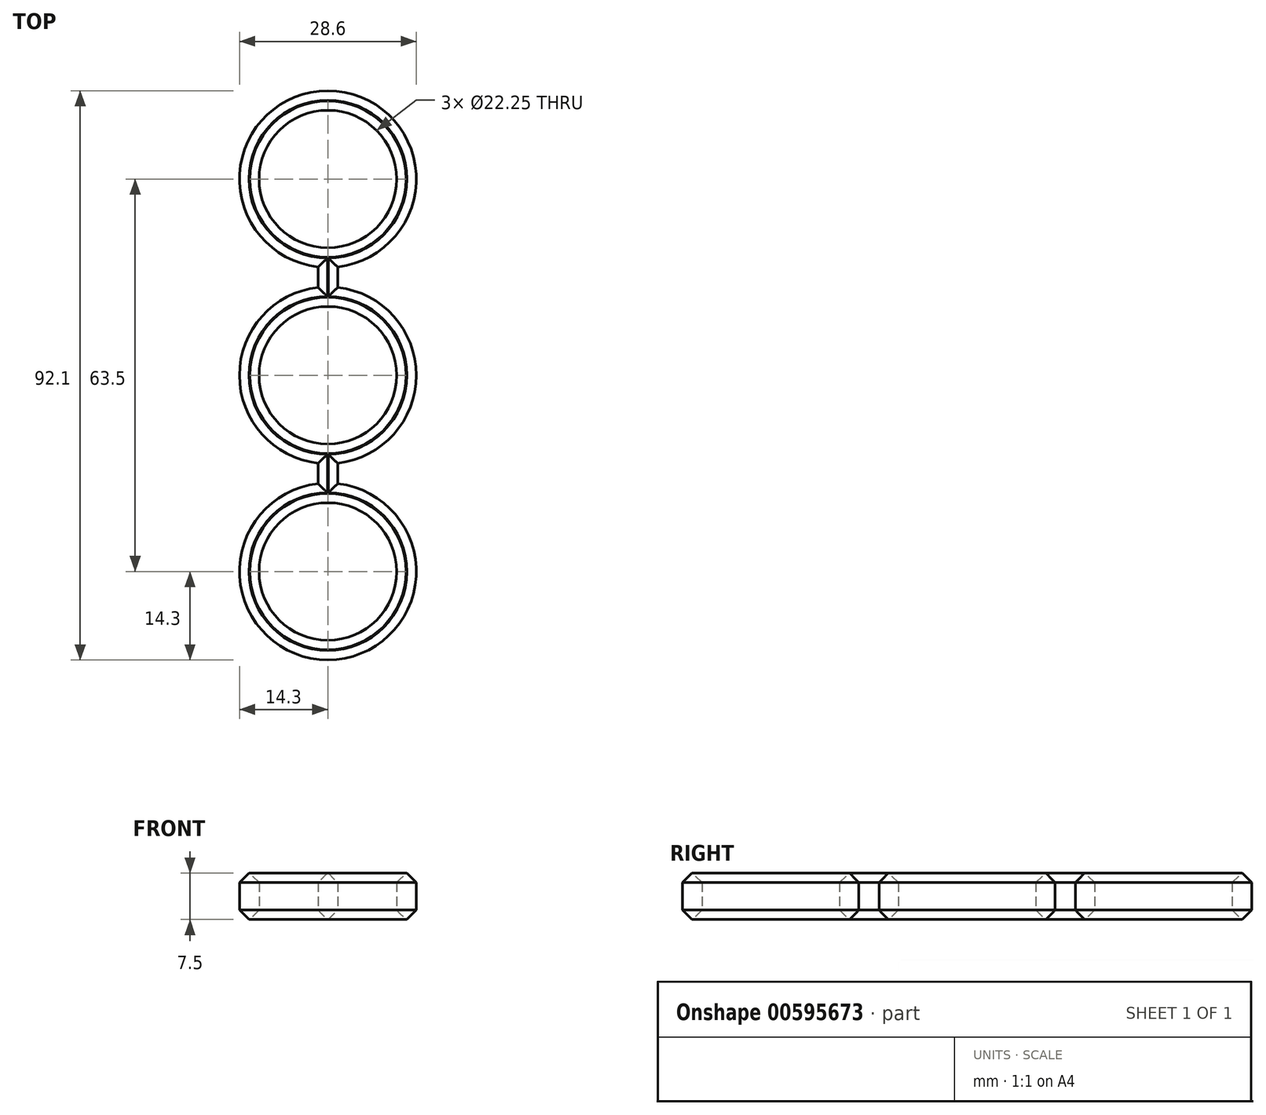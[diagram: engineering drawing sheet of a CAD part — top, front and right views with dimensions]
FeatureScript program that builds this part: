
annotation { "Feature Type Name" : "Feature", "Feature Type Description" : "" }
export const myFeature = defineFeature(function(context is Context, id is Id, definition is map)
    precondition{}
    {
        {
            var Q0;
            Q0=qCreatedBy(makeId("Top.planeOp"),FACE);
            var sketch = newSketch(context, id + "F0", { "sketchPlane" : qUnion([Q0])});
            skCircle(sketch, "E0", {"center": v(0, 0) * mm, "radius": 11.12 * mm});
            skCircle(sketch, "E1", {"center": v(0, 0) * mm, "radius": 14.3 * mm});
            skCircle(sketch, "E2", {"center": v(0, 31.75) * mm, "radius": 11.12 * mm});
            skCircle(sketch, "E3", {"center": v(0, 31.75) * mm, "radius": 14.3 * mm});
            skCircle(sketch, "E4", {"center": v(0, -31.75) * mm, "radius": 11.12 * mm});
            skCircle(sketch, "E5", {"center": v(0, -31.75) * mm, "radius": 14.3 * mm});
            skLineSegment(sketch, "E6.bottom", {"start": v(-1.59, 12.71) * mm, "end": v(1.59, 12.71) * mm});
            skLineSegment(sketch, "E6.top", {"start": v(-1.59, 19.04) * mm, "end": v(1.59, 19.04) * mm});
            skLineSegment(sketch, "E6.left", {"start": v(-1.59, 12.71) * mm, "end": v(-1.59, 19.04) * mm});
            skLineSegment(sketch, "E6.right", {"start": v(1.59, 12.71) * mm, "end": v(1.59, 19.04) * mm});
            skPoint(sketch, "E6.middle", {"position": v(0, 15.88) * mm});
            skLineSegment(sketch, "E7.bottom", {"start": v(-1.59, -19.04) * mm, "end": v(1.59, -19.04) * mm});
            skLineSegment(sketch, "E7.top", {"start": v(-1.59, -12.71) * mm, "end": v(1.59, -12.71) * mm});
            skLineSegment(sketch, "E7.left", {"start": v(-1.59, -19.04) * mm, "end": v(-1.59, -12.71) * mm});
            skLineSegment(sketch, "E7.right", {"start": v(1.59, -19.04) * mm, "end": v(1.59, -12.71) * mm});
            skPoint(sketch, "E7.middle", {"position": v(0, -15.88) * mm});
            skSolve(sketch);
        }
        {
            var Q0;
            Q0 = qSketchRegion(id + "F0", true);
            extrude(context, id + "F1", {"entities" : qUnion([Q0]), "depth" : 7.5 * mm, "offsetDistance" : 25.4 * mm});
        }
        {
            var Q0;
            Q0=makeQuery(id+"F1.opExtrude","CAP_FACE",FACE,{"disambiguationData":[OSD([sQuery(id+"F0.wireOp",EDGE,"E0"),sQuery(id+"F0.wireOp",EDGE,"E1"),sQuery(id+"F0.wireOp",EDGE,"E2"),sQuery(id+"F0.wireOp",EDGE,"E3"),sQuery(id+"F0.wireOp",EDGE,"E4"),sQuery(id+"F0.wireOp",EDGE,"E5"),sQuery(id+"F0.wireOp",EDGE,"E6.left"),sQuery(id+"F0.wireOp",EDGE,"E6.right"),sQuery(id+"F0.wireOp",EDGE,"E7.left"),sQuery(id+"F0.wireOp",EDGE,"E7.right")])],"isStart":false});
            var Q1;
            Q1=makeQuery(id+"F1.opExtrude","CAP_FACE",FACE,{"disambiguationData":[OSD([sQuery(id+"F0.wireOp",EDGE,"E0"),sQuery(id+"F0.wireOp",EDGE,"E1"),sQuery(id+"F0.wireOp",EDGE,"E2"),sQuery(id+"F0.wireOp",EDGE,"E3"),sQuery(id+"F0.wireOp",EDGE,"E4"),sQuery(id+"F0.wireOp",EDGE,"E5"),sQuery(id+"F0.wireOp",EDGE,"E6.left"),sQuery(id+"F0.wireOp",EDGE,"E6.right"),sQuery(id+"F0.wireOp",EDGE,"E7.left"),sQuery(id+"F0.wireOp",EDGE,"E7.right")])],"isStart":true});
            chamfer(context, id + "F2", {"entities" : qUnion([Q0, Q1]), "width" : 1.52 * mm, "tangentPropagation" : true});
        }
    });
